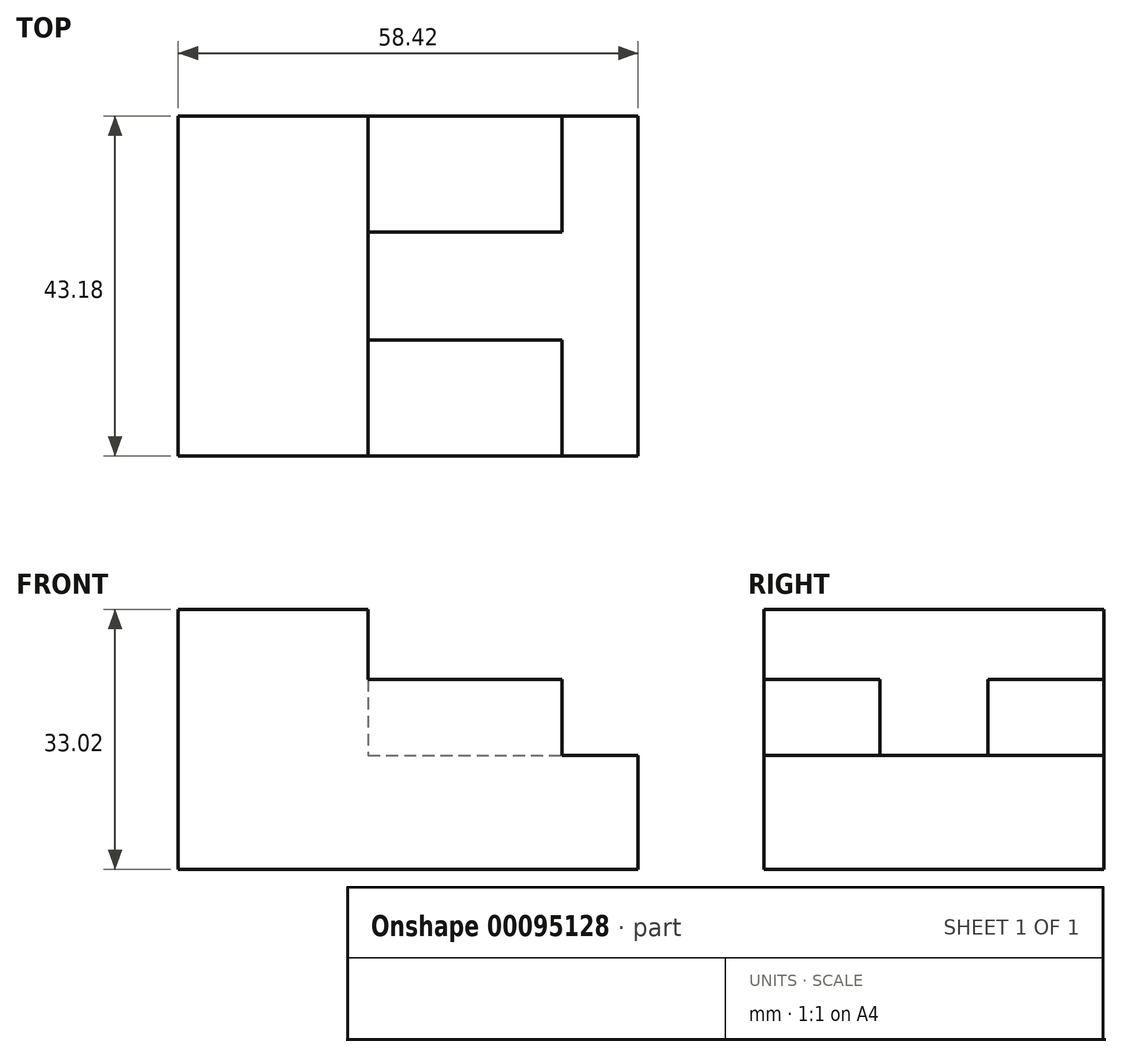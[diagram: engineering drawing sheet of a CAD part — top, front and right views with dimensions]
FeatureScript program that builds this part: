
annotation { "Feature Type Name" : "Feature", "Feature Type Description" : "" }
export const myFeature = defineFeature(function(context is Context, id is Id, definition is map)
    precondition{}
    {
        {
            var Q0;
            Q0=qCreatedBy(makeId("Top.planeOp"),FACE);
            var sketch = newSketch(context, id + "F0", { "sketchPlane" : qUnion([Q0])});
            skLineSegment(sketch, "E0.bottom", {"start": v(-29.2, 21.59) * mm, "end": v(29.21, 21.59) * mm});
            skLineSegment(sketch, "E0.top", {"start": v(-29.21, -21.59) * mm, "end": v(29.2, -21.59) * mm});
            skLineSegment(sketch, "E0.left", {"start": v(-29.2, 21.59) * mm, "end": v(-29.21, -21.59) * mm});
            skLineSegment(sketch, "E0.right", {"start": v(29.21, 21.59) * mm, "end": v(29.2, -21.59) * mm});
            skPoint(sketch, "E0.middle", {"position": v(0, 0) * mm});
            skSolve(sketch);
        }
        {
            var Q0;
            Q0=makeQuery(id+"F0.imprint","IMPRINT",FACE,{"disambiguationData":[TD([[makeQuery(id+"F0.imprint","IMPRINT",EDGE,{"derivedFrom":sQuery(id+"F0.wireOp",EDGE,"E0.bottom")}),-1.0]])]});
            extrude(context, id + "F1", {"entities" : qUnion([Q0]), "depth" : 33.02 * mm});
        }
        {
            var Q0;
            Q0=qCreatedBy(makeId("Front.planeOp"),FACE);
            var sketch = newSketch(context, id + "F2", { "sketchPlane" : qUnion([Q0])});
            skLineSegment(sketch, "E1.bottom", {"start": v(-5.08, 33.02) * mm, "end": v(39.87, 33.02) * mm});
            skLineSegment(sketch, "E1.top", {"start": v(-5.08, 14.48) * mm, "end": v(39.87, 14.48) * mm});
            skLineSegment(sketch, "E1.left", {"start": v(-5.08, 33.02) * mm, "end": v(-5.08, 14.48) * mm});
            skLineSegment(sketch, "E1.right", {"start": v(39.87, 33.02) * mm, "end": v(39.87, 14.48) * mm});
            skSolve(sketch);
        }
        {
            var Q0;
            Q0=makeQuery(id+"F2.imprint","IMPRINT",FACE,{"disambiguationData":[TD([[makeQuery(id+"F2.imprint","IMPRINT",EDGE,{"derivedFrom":sQuery(id+"F2.wireOp",EDGE,"E1.bottom")}),-1.0]])]});
            extrude(context, id + "F3", {"entities" : qUnion([Q0]), "operationType" : NewBodyOperationType.REMOVE, "endBound" : BoundingType.THROUGH_ALL, "oppositeDirection" : true, "depth" : 25.4 * mm});
        }
        {
            var Q0;
            Q0=makeQuery(id+"F3.boolean.opBoolean","COPY",FACE,{"derivedFrom":makeQuery(id+"F3.opExtrude","CAP_FACE",FACE,{"disambiguationData":[OSD([sQuery(id+"F2.wireOp",EDGE,"E1.bottom"),sQuery(id+"F2.wireOp",EDGE,"E1.top"),sQuery(id+"F2.wireOp",EDGE,"E1.left"),sQuery(id+"F2.wireOp",EDGE,"E1.right")])],"isStart":true})});
            extrude(context, id + "F4", {"entities" : qUnion([Q0]), "operationType" : NewBodyOperationType.REMOVE, "endBound" : BoundingType.THROUGH_ALL, "oppositeDirection" : true, "depth" : 25.4 * mm});
        }
        {
            var Q0;
            Q0=qCreatedBy(makeId("Top.planeOp"),FACE);
            var sketch = newSketch(context, id + "F5", { "sketchPlane" : qUnion([Q0])});
            skLineSegment(sketch, "E2.bottom", {"start": v(-5.08, 21.59) * mm, "end": v(19.56, 21.59) * mm});
            skLineSegment(sketch, "E2.top", {"start": v(-5.08, 6.86) * mm, "end": v(19.56, 6.86) * mm});
            skLineSegment(sketch, "E2.left", {"start": v(-5.08, 21.59) * mm, "end": v(-5.08, 6.86) * mm});
            skLineSegment(sketch, "E2.right", {"start": v(19.56, 21.59) * mm, "end": v(19.56, 6.86) * mm});
            skSolve(sketch);
        }
        {
            var Q0;
            Q0=makeQuery(id+"F5.imprint","IMPRINT",FACE,{"disambiguationData":[TD([[makeQuery(id+"F5.imprint","IMPRINT",EDGE,{"derivedFrom":sQuery(id+"F5.wireOp",EDGE,"E2.bottom")}),-1.0]])]});
            extrude(context, id + "F6", {"entities" : qUnion([Q0]), "operationType" : NewBodyOperationType.ADD, "depth" : 24.13 * mm});
        }
        {
            var Q0;
            Q0=qCreatedBy(makeId("Top.planeOp"),FACE);
            var sketch = newSketch(context, id + "F7", { "sketchPlane" : qUnion([Q0])});
            skLineSegment(sketch, "E3.bottom", {"start": v(-5.08, -21.59) * mm, "end": v(19.56, -21.59) * mm});
            skLineSegment(sketch, "E3.top", {"start": v(-5.08, -6.86) * mm, "end": v(19.56, -6.86) * mm});
            skLineSegment(sketch, "E3.left", {"start": v(-5.08, -21.59) * mm, "end": v(-5.08, -6.86) * mm});
            skLineSegment(sketch, "E3.right", {"start": v(19.56, -21.59) * mm, "end": v(19.56, -6.86) * mm});
            skSolve(sketch);
        }
        {
            var Q0;
            Q0=makeQuery(id+"F7.imprint","IMPRINT",FACE,{"disambiguationData":[TD([[makeQuery(id+"F7.imprint","IMPRINT",EDGE,{"derivedFrom":sQuery(id+"F7.wireOp",EDGE,"E3.bottom")}),1.0]])]});
            extrude(context, id + "F8", {"entities" : qUnion([Q0]), "operationType" : NewBodyOperationType.ADD, "depth" : 24.13 * mm});
        }
    });
